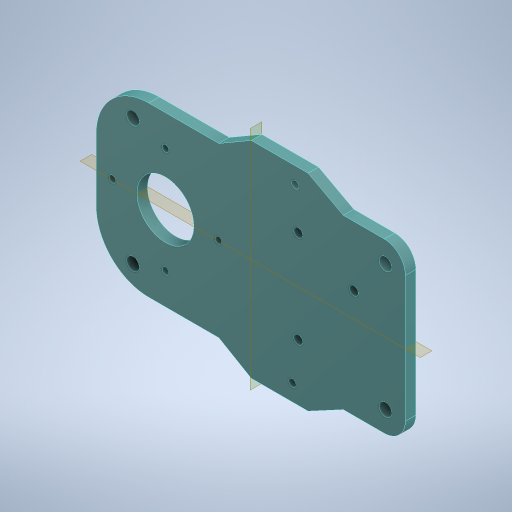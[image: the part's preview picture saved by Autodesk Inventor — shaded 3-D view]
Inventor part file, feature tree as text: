
AUTODESK INVENTOR PART (.ipt)
format: ipt  version: 2024.3 (Build 283343000, 343)  size: 276,992 bytes
history: native  units: in
note: dims shown in document units (in); Inventor stores cm internally (conversion verified against a paired STEP export)
features: plane x2, extrude x2, sketch x2, imported_body x1
ambient origin geometry x8: Origin, YZ Plane, XZ Plane, XY Plane, X Axis, Y Axis, Z Axis, Center Point
bodies: Solid1 (feature_tree)
feature tree (7):
  plane  "Work Plane1"
  plane  "Work Plane2"
  extrude  "Extrusion1"  [1 undecoded]
  extrude  "Extrusion2"  TaperAngle=0.0deg  [1 undecoded]
  sketch  "Sketch3"  dims[d0=-1.9283in d1=-2.8937in]
  sketch  "Sketch4"  dims[d7=0.1654in d8=0.0in d9=0.0in d10=0.1969in d11=0.0in d12=0.4491in]
  imported_body  "Base1"
note: 2 required parameter values undecoded (feature->parameter linkage not recoverable at this tier; creation-order binding heuristic only, values carry confidence <= 0.55)
